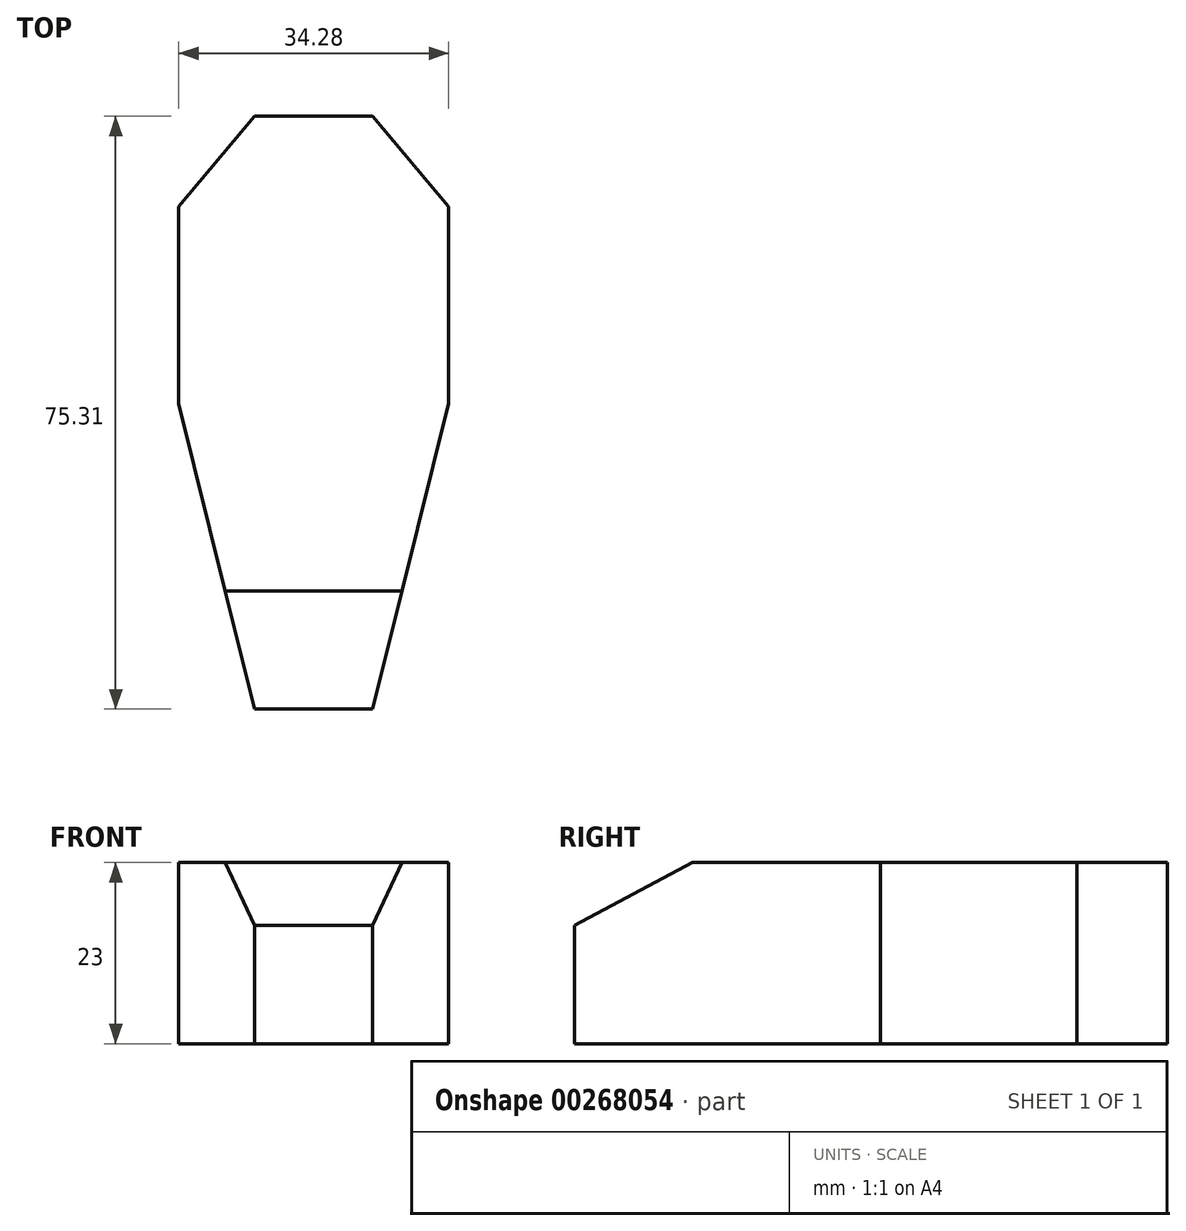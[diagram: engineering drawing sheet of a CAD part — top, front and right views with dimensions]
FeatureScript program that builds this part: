
annotation { "Feature Type Name" : "Feature", "Feature Type Description" : "" }
export const myFeature = defineFeature(function(context is Context, id is Id, definition is map)
    precondition{}
    {
        {
            var Q0;
            Q0=qCreatedBy(makeId("Top.planeOp"),FACE);
            var sketch = newSketch(context, id + "F0", { "sketchPlane" : qUnion([Q0])});
            skLineSegment(sketch, "E0", {"start": v(-7.5, 24) * mm, "end": v(7.5, 24) * mm});
            skLineSegment(sketch, "E1", {"start": v(7.5, 24) * mm, "end": v(17.14, 12.5) * mm});
            skLineSegment(sketch, "E2", {"start": v(17.14, 12.5) * mm, "end": v(17.14, -12.5) * mm});
            skLineSegment(sketch, "E3", {"start": v(17.14, -12.5) * mm, "end": v(7.5, -51.32) * mm});
            skLineSegment(sketch, "E4", {"start": v(7.5, -51.32) * mm, "end": v(-7.5, -51.32) * mm});
            skLineSegment(sketch, "E5", {"start": v(-7.5, -51.32) * mm, "end": v(-17.14, -12.5) * mm});
            skLineSegment(sketch, "E6", {"start": v(-17.14, -12.5) * mm, "end": v(-17.14, 12.5) * mm});
            skLineSegment(sketch, "E7", {"start": v(-17.14, 12.5) * mm, "end": v(-7.5, 24) * mm});
            skLineSegment(sketch, "E8", {"start": v(0, 24) * mm, "end": v(0, -51.32) * mm, "construction": true});
            skLineSegment(sketch, "E9", {"start": v(-17.14, 0) * mm, "end": v(17.14, 0) * mm, "construction": true});
            skPoint(sketch, "E10", {"position": v(0, 0) * mm});
            skSolve(sketch);
        }
        {
            var Q0;
            Q0=makeQuery(id+"F0.imprint","IMPRINT",FACE,{"disambiguationData":[TD([[makeQuery(id+"F0.imprint","IMPRINT",EDGE,{"derivedFrom":sQuery(id+"F0.wireOp",EDGE,"E0")}),-1.0]])]});
            extrude(context, id + "F1", {"entities" : qUnion([Q0]), "depth" : 23 * mm});
        }
        {
            var Q0;
            Q0=makeQuery(id+"F1.opExtrude","SWEPT_FACE",FACE,{"disambiguationData":[OSD([sQuery(id+"F0.wireOp",EDGE,"E6")])]});
            var sketch = newSketch(context, id + "F2", { "sketchPlane" : qUnion([Q0])});
            skLineSegment(sketch, "E11", {"start": v(51.32, 15) * mm, "end": v(51.32, 23) * mm});
            skLineSegment(sketch, "E12", {"start": v(51.32, 15) * mm, "end": v(36.32, 23) * mm});
            skLineSegment(sketch, "E13", {"start": v(36.32, 23) * mm, "end": v(51.32, 23) * mm});
            skSolve(sketch);
        }
        {
            var Q0;
            Q0 = qSketchRegion(id + "F2", true);
            extrude(context, id + "F3", {"entities" : qUnion([Q0]), "operationType" : NewBodyOperationType.REMOVE, "oppositeDirection" : true, "depth" : 35 * mm});
        }
    });
